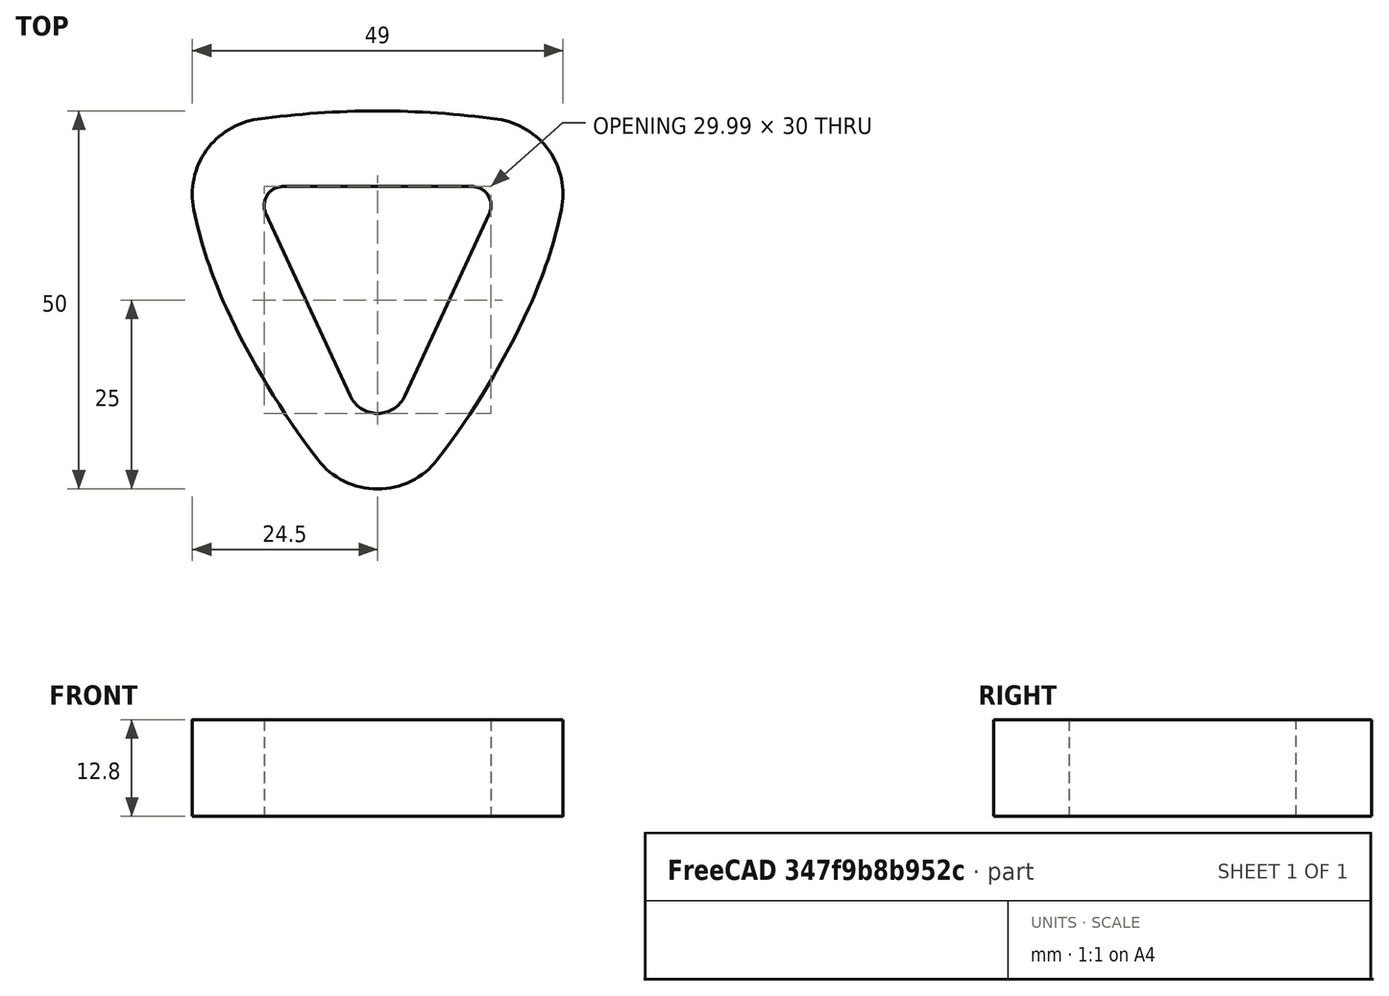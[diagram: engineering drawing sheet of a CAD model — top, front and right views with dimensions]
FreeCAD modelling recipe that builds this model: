
FCSTD DOCUMENT  (FreeCAD 1.0R39109 (Git))
Label: Stator_Coil_Triangular_Reduced
License: All rights reserved
LicenseURL: http://en.wikipedia.org/wiki/All_rights_reserved
objects: Sketcher::SketchObject×1, PartDesign::Pad×1, PartDesign::Body×1, Spreadsheet::Sheet×1
note: 6 computed .brp shape members not serialized (recipe doc carries the construction recipe); baked Part::Feature solids carry a one-line shape summary decoded from their .brp
EXTERNAL_REF file=../../Master_of_Puppets.FCStd obj=Alternator
EXTERNAL_REF file=../../Master_of_Puppets.FCStd obj=Spreadsheet

FEATURE [Sketcher::SketchObject] Sketch
  ArcFitTolerance = 0
  AttachmentSupport = -> [XY_Plane]
  FullyConstrained = true
  MakeInternals = false
  MapMode = 5
  expr: Constraints[25] = Spreadsheet.CoilLegWidth
  expr: Constraints[27] = Spreadsheet.CoilLegWidth
  expr: Constraints[2] = Spreadsheet.CoilWinderPinRadius
  expr: Constraints[33] = Spreadsheet.CornerCircleRadius
  expr: Constraints[34] = Spreadsheet.CornerCircleRadius
  expr: Constraints[35] = Spreadsheet.CornerCircleRadius
  expr: Constraints[60] = Spreadsheet.CoilLegWidth
  expr: Constraints[61] = Spreadsheet.VerticalDimension
  expr: Constraints[63] = Spreadsheet.HorizontalDistanceBetweenPins
  expr: Constraints[6] = Spreadsheet.InnerBottomArcRadius
  sketch-geometry (24):
    g0: Circle [constr] CenterX=0 CenterY=18.125 CenterZ=0 NormalX=0 NormalY=0 NormalZ=1 AngleXU=0 Radius=18.125
    g1: Circle [constr] CenterX=-12.5 CenterY=27.5 CenterZ=0 NormalX=0 NormalY=0 NormalZ=1 AngleXU=0 Radius=2.5
    g2: Circle [constr] CenterX=12.5 CenterY=27.5 CenterZ=0 NormalX=0 NormalY=0 NormalZ=1 AngleXU=0 Radius=2.5
    g3: Circle [constr] CenterX=0 CenterY=4 CenterZ=0 NormalX=0 NormalY=0 NormalZ=1 AngleXU=0 Radius=4
    g4: LineSegment StartX=3.63174 StartY=2.32355 StartZ=0 EndX=14.7698 EndY=26.4522 EndZ=0
    g5: LineSegment StartX=-12.5 StartY=30 StartZ=0 EndX=12.5 EndY=30 EndZ=0
    g6: LineSegment StartX=-3.63174 StartY=2.32355 StartZ=0 EndX=-14.7698 EndY=26.4522 EndZ=0
    g7: ArcOfCircle CenterX=-12.5 CenterY=27.5 CenterZ=0 NormalX=0 NormalY=0 NormalZ=1 AngleXU=0 Radius=2.5 StartAngle=1.5708 EndAngle=3.57406
    g8: ArcOfCircle CenterX=12.5 CenterY=27.5 CenterZ=0 NormalX=0 NormalY=0 NormalZ=1 AngleXU=0 Radius=2.5 StartAngle=5.85072 EndAngle=7.85398
    g9: ArcOfCircle CenterX=0 CenterY=4 CenterZ=0 NormalX=0 NormalY=0 NormalZ=1 AngleXU=0 Radius=4 StartAngle=3.57406 EndAngle=5.85072
    g10: LineSegment [constr] StartX=10.9259 StartY=18.125 StartZ=0 EndX=20.0052 EndY=13.9339 EndZ=0
    g11: LineSegment [constr] StartX=-10.9259 StartY=18.125 StartZ=0 EndX=-20.0052 EndY=13.9339 EndZ=0
    g12: Circle [constr] CenterX=-14.5 CenterY=29 CenterZ=0 NormalX=0 NormalY=0 NormalZ=1 AngleXU=0 Radius=10
    g13: Circle [constr] CenterX=14.5 CenterY=29 CenterZ=0 NormalX=0 NormalY=0 NormalZ=1 AngleXU=0 Radius=10
    g14: ArcOfCircle CenterX=34.3876 CenterY=39.0423 CenterZ=0 NormalX=0 NormalY=0 NormalZ=1 AngleXU=0 Radius=59.9083 StartAngle=3.34419 EndAngle=3.57406
    g15: ArcOfCircle CenterX=-14.5 CenterY=29 CenterZ=0 NormalX=0 NormalY=0 NormalZ=1 AngleXU=0 Radius=10 StartAngle=1.70851 EndAngle=3.34419
    g16: ArcOfCircle CenterX=76.5816 CenterY=58.5195 CenterZ=0 NormalX=0 NormalY=0 NormalZ=1 AngleXU=0 Radius=106.381 StartAngle=3.57406 EndAngle=3.79409
    g17: Circle [constr] CenterX=0 CenterY=0 CenterZ=0 NormalX=0 NormalY=0 NormalZ=1 AngleXU=0 Radius=10
    g18: ArcOfCircle CenterX=0 CenterY=0 CenterZ=0 NormalX=0 NormalY=0 NormalZ=1 AngleXU=0 Radius=10 StartAngle=3.79409 EndAngle=5.63069
    g19: ArcOfCircle CenterX=-34.3877 CenterY=39.0423 CenterZ=0 NormalX=0 NormalY=0 NormalZ=1 AngleXU=0 Radius=59.9085 StartAngle=5.85072 EndAngle=6.08059
    g20: ArcOfCircle CenterX=14.5 CenterY=29 CenterZ=0 NormalX=0 NormalY=0 NormalZ=1 AngleXU=0 Radius=10 StartAngle=6.08059 EndAngle=7.71627
    g21: ArcOfCircle CenterX=-76.5816 CenterY=58.5195 CenterZ=0 NormalX=0 NormalY=0 NormalZ=1 AngleXU=0 Radius=106.381 StartAngle=5.63069 EndAngle=5.85072
    g22: ArcOfCircle CenterX=0 CenterY=-75.6253 CenterZ=0 NormalX=0 NormalY=0 NormalZ=1 AngleXU=0 Radius=115.625 StartAngle=1.5708 EndAngle=1.70851
    g23: ArcOfCircle CenterX=0 CenterY=-75.6249 CenterZ=0 NormalX=0 NormalY=0 NormalZ=1 AngleXU=0 Radius=115.625 StartAngle=1.43308 EndAngle=1.5708
  constraints (64):
    c: PointOnObject(g13,g0)
    c: PointOnObject(g12,g0)
    c: Radius(g1) = 2.5
    c: PointOnObject(g12,g1)
    c: Equal(g2,g1)
    c: Tangent(g2,g0)
    c: Radius(g3) = 4
    c: Tangent(g4,g2) = -1.5708
    c: Tangent(g6,g1) = 1.5708
    c: Coincident(g7,g6)
    c: Coincident(g8,g2)
    c: Coincident(g8,g4)
    c: Coincident(g9,g3)
    c: Coincident(g5,g7)
    c: Coincident(g8,g5)
    c: Horizontal(g5)
    c: Vertical(g7,g5)
    c: Vertical(g8,g5)
    c: Vertical(g0,g9)
    c: Equal(g9,g3)
    c: Tangent(g9,g6) = 1.5708
    c: Tangent(g4,g9) = -1.5708
    c: Tangent(g5,g1) = 1.5708
    c: Tangent(g0,g7)
    c: PointOnObject(g10,g4)
    c: Distance(g10) = 10
    c: PointOnObject(g11,g6)
    c: Distance(g11) = 10
    c: Horizontal(g11,g0)
    c: Horizontal(g10,g0)
    c: Perpendicular(g6,g11)
    c: Perpendicular(g4,g10)
    c: PointOnObject(g22,g-2)
    c: Radius(g12) = 10
    c: Radius(g13) = 10
    c: Radius(g17) = 10
    c: Tangent(g16,g17) = -1.5708
    c: Coincident(g18,g16)
    c: Tangent(g21,g18) = -1.5708
    c: Tangent(g15,g14) = -1.5708
    c: Tangent(g19,g20) = -1.5708
    c: Tangent(g22,g15) = -1.5708
    c: PointOnObject(g14,g12)
    c: Tangent(g23,g20) = -1.5708
    c: PointOnObject(g19,g13)
    c: Coincident(g16,g11)
    c: Perpendicular(g16,g11)
    c: Tangent(g14,g16) = -1.5708
    c: Tangent(g19,g21) = -1.5708
    c: Coincident(g19,g10)
    c: Perpendicular(g21,g10)
    c: Tangent(g23,g22) = -1.5708
    c: Coincident(g-1,g18)
    c: Coincident(g17,g18)
    c: PointOnObject(g9,g-2)
    c: Coincident(g20,g13)
    c: Coincident(g15,g12)
    c: PointOnObject(g20,g8)
    c: PointOnObject(g18,g9)
    c: PointOnObject(g18,g0)
    c: Distance(g22,g5) = 10
    c: Distance(g18,g5) = 30
    c: Perpendicular(g22,g-2)
    c: DistanceX(g7,g8) = 25
FEATURE [PartDesign::Pad] Pad
  AllowMultiFace = false
  Direction = (0,0,1)
  Length = 12.8
  Length2 = 100
  Profile = -> Sketch
  Suppressed = false
  Type = 0
  expr: Length = Spreadsheet.CoilThickness
FEATURE [PartDesign::Body] Body  label="Stator_Coil"
  AllowCompound = false
  Group = -> [Sketch,Pad]
  Origin = -> Origin
  Tip = -> Pad
FEATURE [Spreadsheet::Sheet] Spreadsheet
  cells = A1='Inputs; A2='CoilHoleWidthAtOuterRadius; B2(CoilHoleWidthAtOuterRadius)==Master_of_Puppets#Spreadsheet.CoilHoleWidthAtOuterRadius; A3='CoilHoleWidthAtInnerRadius; B3(CoilHoleWidthAtInnerRadius)==Master_of_Puppets#Spreadsheet.CoilHoleWidthAtInnerRadius; A4='MagnetWidth; B4(MagnetWidth)==Master_of_Puppets#Spreadsheet.MagnetWidth; A5='MagnetLength; B5(MagnetLength)==Master_of_Puppets#Spreadsheet.MagnetLength; A6='CoilType; B6(CoilType)==Master_of_Puppets#Spreadsheet.CoilType; A7='SmallestMagnetDimension; B7(SmallestMagnetDimension)==Master_of_Puppets#Alternator.SmallestMagnetDimension; A8='CoilLegWidth; B8(CoilLegWidth)==CoilType != 3 ? SmallestMagnetDimension / 2 : Master_of_Puppets#Spreadsheet.CoilLegWidth; C8='Prevent this from breaking when not triangular coils; A9='CoilWinderPinRadius; B9(CoilWinderPinRadius)==Master_of_Puppets#Alternator.CoilWinderPinRadius; A10='CoilThickness; B10(CoilThickness)==Master_of_Puppets#Alternator.CoilThickness; A11='CoilLegWidthReduced; B11(CoilLegWidthReduced)==Master_of_Puppets#Alternator.CoilLegWidthReduced; A12='HorizontalDistanceBetweenPins; B12(HorizontalDistanceBetweenPins)==Master_of_Puppets#Alternator.TriangularHorizontalDistanceBetweenPins; A13='LargestMagnetDimension; B13(LargestMagnetDimension)==Master_of_Puppets#Alternator.LargestMagnetDimension; A14='Calculated; A15='CornerCircleRadius; B15(CornerCircleRadius)==CoilType != 3 ? CoilLegWidth : CoilLegWidthReduced; C15='Prevent this from breaking when not triangular coils; A16='InnerBottomArcRadius; B16(InnerBottomArcRadius)==CoilType == 3 ? CoilHoleWidthAtInnerRadius / 2 : 4; C16='Duplicated in Stator_Coil_Triangular_Reduced; A17='VerticalDimension; B17(VerticalDimension)==CoilType != 3 ? LargestMagnetDimension : MagnetLength; C17='Prevent this from breaking when not triangular coils
